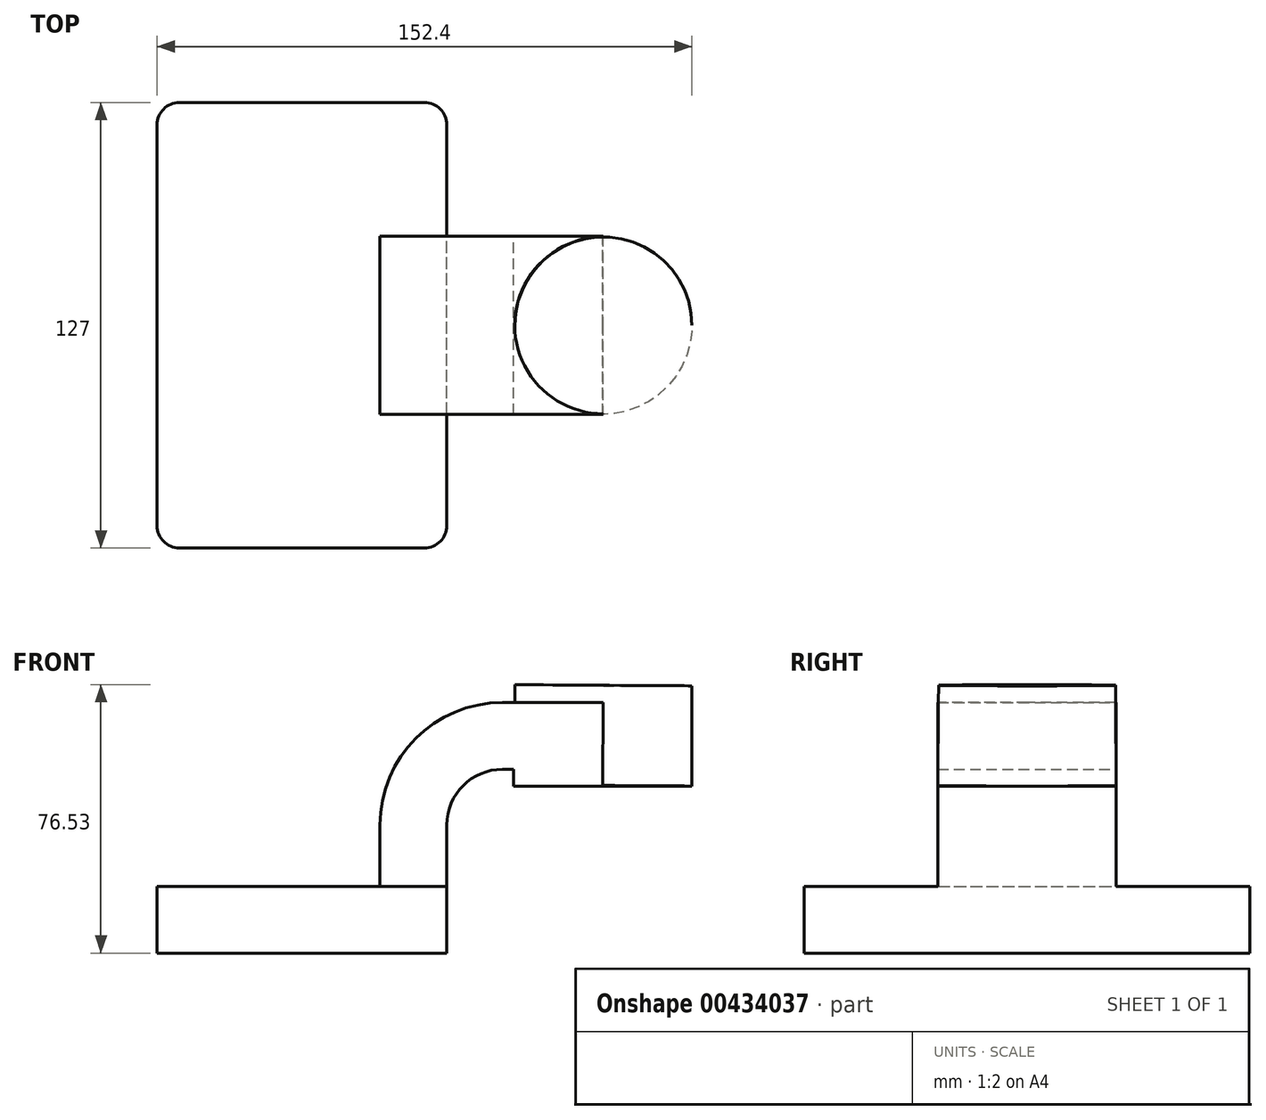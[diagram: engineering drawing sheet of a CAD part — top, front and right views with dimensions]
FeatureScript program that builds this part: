
annotation { "Feature Type Name" : "Feature", "Feature Type Description" : "" }
export const myFeature = defineFeature(function(context is Context, id is Id, definition is map)
    precondition{}
    {
        {
            var Q0;
            Q0=qCreatedBy(makeId("Front.planeOp"),FACE);
            var sketch = newSketch(context, id + "F0", { "sketchPlane" : qUnion([Q0])});
            skLineSegment(sketch, "E0.bottom", {"start": v(-41.28, -9.53) * mm, "end": v(41.28, -9.53) * mm});
            skLineSegment(sketch, "E0.top", {"start": v(-41.28, 9.53) * mm, "end": v(41.28, 9.53) * mm});
            skLineSegment(sketch, "E0.left", {"start": v(-41.28, -9.53) * mm, "end": v(-41.28, 9.53) * mm});
            skLineSegment(sketch, "E0.right", {"start": v(41.28, -9.53) * mm, "end": v(41.28, 9.53) * mm});
            skPoint(sketch, "E0.middle", {"position": v(0, 0) * mm});
            skLineSegment(sketch, "E1.bottom", {"start": v(60.32, 66.67) * mm, "end": v(111.12, 66.67) * mm});
            skLineSegment(sketch, "E1.top", {"start": v(60.32, 38.1) * mm, "end": v(111.12, 38.1) * mm});
            skLineSegment(sketch, "E1.left", {"start": v(60.32, 66.67) * mm, "end": v(60.32, 38.1) * mm});
            skLineSegment(sketch, "E1.right", {"start": v(111.12, 66.67) * mm, "end": v(111.12, 38.1) * mm});
            skPoint(sketch, "E1.middle", {"position": v(85.72, 52.39) * mm});
            skLineSegment(sketch, "E2", {"start": v(41.28, 9.53) * mm, "end": v(41.28, 27) * mm});
            skArc(sketch, "E3", {"start": v(41.27, 27) * mm, "mid": v(45.92, 38.23) * mm, "end": v(57.15, 42.88) * mm});
            skLineSegment(sketch, "E4", {"start": v(57.15, 42.88) * mm, "end": v(75.88, 42.88) * mm});
            skLineSegment(sketch, "E5.0", {"start": v(57.15, 61.93) * mm, "end": v(75.88, 61.93) * mm});
            skArc(sketch, "E5.1", {"start": v(22.22, 27) * mm, "mid": v(32.45, 51.7) * mm, "end": v(57.15, 61.93) * mm});
            skLineSegment(sketch, "E5.2", {"start": v(22.22, 9.53) * mm, "end": v(22.22, 27) * mm});
            skFitSpline(sketch, "E6", {"points": [v(-41.28, 9.52) * mm, v(57.15, 61.93) * mm], "startDerivative": vector(1.35, 95.03) * mm, "endDerivative": vector(94.51, -2.11) * mm});
            skLineSegment(sketch, "E7", {"start": v(75.88, 42.88) * mm, "end": v(85.72, 42.88) * mm});
            skLineSegment(sketch, "E8", {"start": v(75.88, 61.93) * mm, "end": v(85.9, 61.93) * mm});
            skLineSegment(sketch, "E9", {"start": v(85.72, 38.1) * mm, "end": v(85.9, 66.67) * mm});
            skSolve(sketch);
        }
        {
            var Q0;
            Q0=makeQuery(id+"F0.imprint","IMPRINT",FACE,{"disambiguationData":[TD([[makeQuery(id+"F0.imprint","IMPRINT",EDGE,{"derivedFrom":sQuery(id+"F0.wireOp",EDGE,"E0.bottom")}),1.0]])]});
            extrude(context, id + "F1", {"entities" : qUnion([Q0]), "endBound" : BoundingType.SYMMETRIC, "depth" : 127 * mm});
        }
        {
            var Q0;
            {var subQ1=sQuery(id+"F0.wireOp",EDGE,"E2");Q0=makeQuery(id+"F0.imprint","IMPRINT",FACE,{"disambiguationData":[TD([[makeQuery(id+"F0.imprint","IMPRINT",EDGE,{"derivedFrom":subQ1}),1.0]])]});}
            var Q1;
            {var subQ0=sQuery(id+"F0.wireOp",EDGE,"E1.left");var subQ1=sQuery(id+"F0.wireOp",EDGE,"E1.top");var subQ2=makeQuery(id+"F0.imprint","INTERSECT",VERTEX,{"derivedFrom":[subQ1,subQ0]});Q1=makeQuery(id+"F0.imprint","IMPRINT",FACE,{"disambiguationData":[TD([[makeQuery(id+"F0.imprint","IMPRINT",EDGE,{"disambiguationData":[TD([[subQ2,-1.0]])],"derivedFrom":subQ1}),1.0]])]});}
            extrude(context, id + "F2", {"entities" : qUnion([Q0, Q1]), "operationType" : NewBodyOperationType.ADD, "endBound" : BoundingType.SYMMETRIC, "depth" : 50.8 * mm});
        }
        {
            var Q0;
            Q0=makeQuery(id+"F0.imprint","IMPRINT",FACE,{"disambiguationData":[TD([[makeQuery(id+"F0.imprint","IMPRINT",EDGE,{"derivedFrom":sQuery(id+"F0.wireOp",EDGE,"E5.1")}),1.0]])]});
            extrude(context, id + "F3", {"entities" : qUnion([Q0]), "operationType" : NewBodyOperationType.ADD, "endBound" : BoundingType.SYMMETRIC, "depth" : 15.88 * mm});
        }
        {
            var Q0;
            {var subQ4=sQuery(id+"F0.wireOp",EDGE,"E1.right");Q0=makeQuery(id+"F0.imprint","IMPRINT",FACE,{"disambiguationData":[TD([[makeQuery(id+"F0.imprint","IMPRINT",EDGE,{"derivedFrom":subQ4}),-1.0]])]});}
            var Q1;
            Q1=sQuery(id+"F0.wireOp",EDGE,"E9");
            revolve(context, id + "F4", {"operationType" : NewBodyOperationType.ADD, "entities" : qUnion([Q0]), "axis" : qUnion([Q1]), "revolveType" : RevolveType.FULL});
        }
        {
            var Q0;
            Q0=makeQuery(id+"F1.opExtrude","CAP_EDGE",EDGE,{"disambiguationData":[OSD([sQuery(id+"F0.wireOp",EDGE,"E0.right")])],"isStart":false});
            var Q1;
            Q1=makeQuery(id+"F1.opExtrude","CAP_EDGE",EDGE,{"disambiguationData":[OSD([sQuery(id+"F0.wireOp",EDGE,"E0.left")])],"isStart":false});
            var Q2;
            Q2=makeQuery(id+"F1.opExtrude","CAP_EDGE",EDGE,{"disambiguationData":[OSD([sQuery(id+"F0.wireOp",EDGE,"E0.right")])],"isStart":true});
            var Q3;
            Q3=makeQuery(id+"F1.opExtrude","CAP_EDGE",EDGE,{"disambiguationData":[OSD([sQuery(id+"F0.wireOp",EDGE,"E0.left")])],"isStart":true});
            fillet(context, id + "F5", {"entities" : qUnion([Q0, Q1, Q2, Q3]), "radius" : 6.35 * mm, "tangentPropagation" : true, "allowEdgeOverflow" : false});
        }
    });
